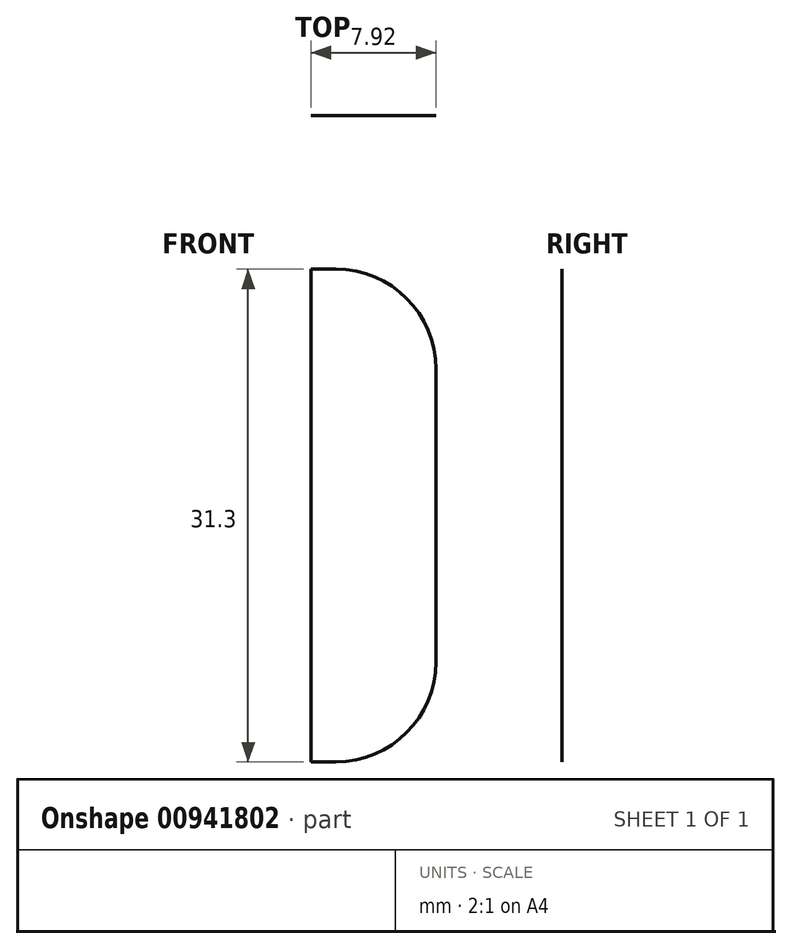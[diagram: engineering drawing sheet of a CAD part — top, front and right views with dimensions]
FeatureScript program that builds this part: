
annotation { "Feature Type Name" : "Feature", "Feature Type Description" : "" }
export const myFeature = defineFeature(function(context is Context, id is Id, definition is map)
    precondition{}
    {
        {
            var Q0;
            Q0=qCreatedBy(makeId("Front.planeOp"),FACE);
            var sketch = newSketch(context, id + "F0", { "sketchPlane" : qUnion([Q0])});
            skLineSegment(sketch, "E0.bottom", {"start": v(0, 0) * mm, "end": v(1.57, 0) * mm});
            skLineSegment(sketch, "E0.top", {"start": v(0, -31.3) * mm, "end": v(1.57, -31.3) * mm});
            skLineSegment(sketch, "E0.left", {"start": v(0, 0) * mm, "end": v(0, -31.3) * mm});
            skLineSegment(sketch, "E0.right", {"start": v(7.92, -6.35) * mm, "end": v(7.92, -24.95) * mm});
            skPoint(sketch, "E1.visualSharp", {"position": v(7.92, 0) * mm});
            skArc(sketch, "E1.filletArc", {"start": v(7.92, -6.35) * mm, "mid": v(6.06, -1.86) * mm, "end": v(1.57, 0) * mm});
            skPoint(sketch, "E2.visualSharp", {"position": v(7.92, -31.3) * mm});
            skArc(sketch, "E2.filletArc", {"start": v(1.57, -31.3) * mm, "mid": v(6.06, -29.44) * mm, "end": v(7.92, -24.95) * mm});
            skSolve(sketch);
        }
        {
            var Q0;
            Q0=qSketchRegion(id+"F0",true);
            extrude(context, id + "F1", {"entities" : qUnion([Q0]), "depth" : 0 * mm, "offsetDistance" : 25.4 * mm});
        }
    });
